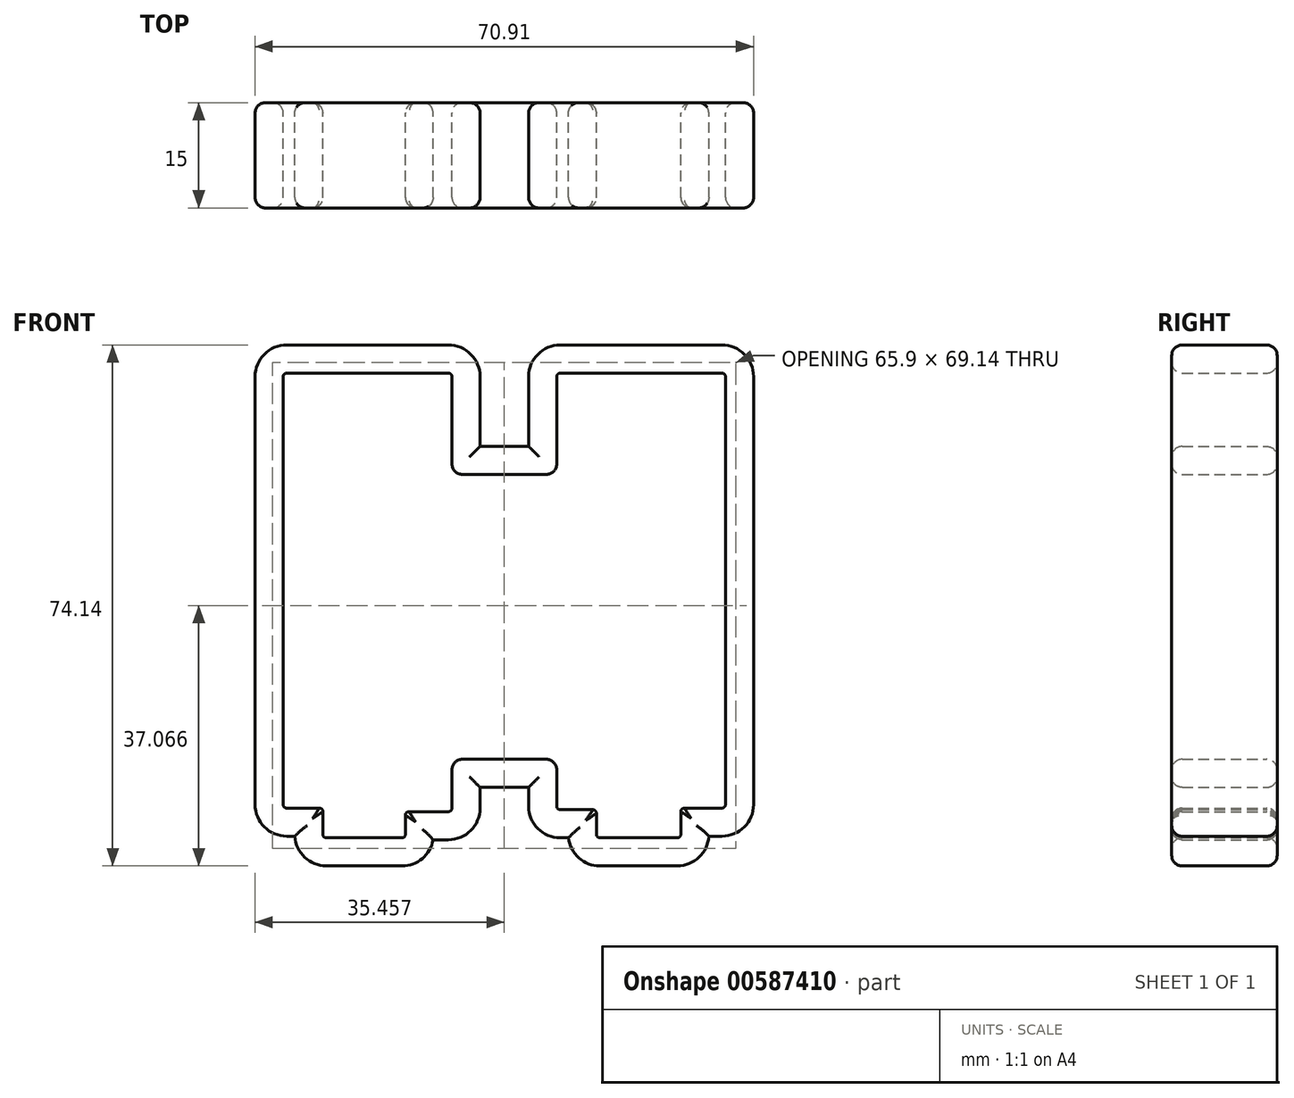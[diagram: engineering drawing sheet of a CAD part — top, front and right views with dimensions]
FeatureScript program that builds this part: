
annotation { "Feature Type Name" : "Feature", "Feature Type Description" : "" }
export const myFeature = defineFeature(function(context is Context, id is Id, definition is map)
    precondition{}
    {
        {
            var Q0;
            Q0=qCreatedBy(makeId("Front.planeOp"),FACE);
            var sketch = newSketch(context, id + "F0", { "sketchPlane" : qUnion([Q0])});
            skLineSegment(sketch, "E0.bottom", {"start": v(-102.27, 13.12) * mm, "end": v(-125.27, 13.12) * mm});
            skLineSegment(sketch, "E0.top", {"start": v(-108.88, -53.02) * mm, "end": v(-119.62, -53.02) * mm});
            skLineSegment(sketch, "E0.left", {"start": v(-101.77, 12.62) * mm, "end": v(-101.77, -48.8) * mm});
            skLineSegment(sketch, "E0.right", {"start": v(-125.77, 12.62) * mm, "end": v(-125.77, -48.28) * mm});
            skLineSegment(sketch, "E1.right", {"start": v(-86.86, -1.3) * mm, "end": v(-86.86, -41.84) * mm});
            skLineSegment(sketch, "E2", {"start": v(-86.86, -1.3) * mm, "end": v(-86.86, 12.62) * mm});
            skLineSegment(sketch, "E3", {"start": v(-86.36, 13.12) * mm, "end": v(-63.36, 13.12) * mm});
            skLineSegment(sketch, "E4", {"start": v(-62.86, 12.62) * mm, "end": v(-62.86, -48.28) * mm});
            skLineSegment(sketch, "E5", {"start": v(-69.71, -53.02) * mm, "end": v(-80.71, -53.02) * mm});
            skLineSegment(sketch, "E6", {"start": v(-86.86, -48.52) * mm, "end": v(-86.86, -41.84) * mm});
            skPoint(sketch, "E7.endSnap0", {"position": v(-113.77, -53.02) * mm});
            skLineSegment(sketch, "E8", {"start": v(-120.12, -49.28) * mm, "end": v(-120.12, -52.52) * mm});
            skLineSegment(sketch, "E9", {"start": v(-108.38, -49.8) * mm, "end": v(-108.38, -52.52) * mm});
            skLineSegment(sketch, "E10", {"start": v(-120.62, -48.78) * mm, "end": v(-125.27, -48.78) * mm});
            skLineSegment(sketch, "E11", {"start": v(-107.88, -49.3) * mm, "end": v(-102.27, -49.3) * mm});
            skPoint(sketch, "E12.orphan", {"position": v(-101.77, -53.02) * mm});
            skPoint(sketch, "E13.orphan", {"position": v(-125.77, -53.02) * mm});
            skPoint(sketch, "E7.end.orphan", {"position": v(-113.77, -49.02) * mm});
            skPoint(sketch, "E7.start.orphan", {"position": v(-113.77, -53.02) * mm});
            skPoint(sketch, "E14.visualSharp", {"position": v(-108.38, -53.02) * mm});
            skArc(sketch, "E14.filletArc", {"start": v(-108.88, -53.02) * mm, "mid": v(-108.53, -52.88) * mm, "end": v(-108.38, -52.52) * mm});
            skPoint(sketch, "E15.visualSharp", {"position": v(-120.12, -53.02) * mm});
            skArc(sketch, "E15.filletArc", {"start": v(-120.12, -52.52) * mm, "mid": v(-119.97, -52.88) * mm, "end": v(-119.62, -53.02) * mm});
            skPoint(sketch, "E16.visualSharp", {"position": v(-120.12, -48.78) * mm});
            skArc(sketch, "E16.filletArc", {"start": v(-120.12, -49.28) * mm, "mid": v(-120.26, -48.93) * mm, "end": v(-120.62, -48.78) * mm});
            skPoint(sketch, "E17.visualSharp", {"position": v(-108.38, -49.3) * mm});
            skArc(sketch, "E17.filletArc", {"start": v(-107.88, -49.3) * mm, "mid": v(-108.24, -49.44) * mm, "end": v(-108.38, -49.8) * mm});
            skPoint(sketch, "E18.visualSharp", {"position": v(-101.77, -49.3) * mm});
            skArc(sketch, "E18.filletArc", {"start": v(-102.27, -49.3) * mm, "mid": v(-101.91, -49.14) * mm, "end": v(-101.77, -48.8) * mm});
            skPoint(sketch, "E19.visualSharp", {"position": v(-125.77, -48.78) * mm});
            skArc(sketch, "E19.filletArc", {"start": v(-125.77, -48.28) * mm, "mid": v(-125.62, -48.64) * mm, "end": v(-125.27, -48.78) * mm});
            skPoint(sketch, "E20.visualSharp", {"position": v(-101.77, 13.12) * mm});
            skArc(sketch, "E20.filletArc", {"start": v(-101.77, 12.62) * mm, "mid": v(-101.91, 12.97) * mm, "end": v(-102.27, 13.12) * mm});
            skPoint(sketch, "E21.visualSharp", {"position": v(-125.77, 13.12) * mm});
            skArc(sketch, "E21.filletArc", {"start": v(-125.27, 13.12) * mm, "mid": v(-125.62, 12.97) * mm, "end": v(-125.77, 12.62) * mm});
            skPoint(sketch, "E22.visualSharp", {"position": v(-86.86, 13.12) * mm});
            skArc(sketch, "E22.filletArc", {"start": v(-86.36, 13.12) * mm, "mid": v(-86.71, 12.97) * mm, "end": v(-86.86, 12.62) * mm});
            skPoint(sketch, "E23.visualSharp", {"position": v(-62.86, 13.12) * mm});
            skArc(sketch, "E23.filletArc", {"start": v(-62.86, 12.62) * mm, "mid": v(-63, 12.97) * mm, "end": v(-63.36, 13.12) * mm});
            skLineSegment(sketch, "E24", {"start": v(-81.21, -49.52) * mm, "end": v(-81.21, -52.52) * mm});
            skLineSegment(sketch, "E25", {"start": v(-69.21, -49.28) * mm, "end": v(-69.21, -52.52) * mm});
            skLineSegment(sketch, "E26", {"start": v(-81.71, -49.02) * mm, "end": v(-86.36, -49.02) * mm});
            skLineSegment(sketch, "E27", {"start": v(-68.71, -48.78) * mm, "end": v(-63.36, -48.78) * mm});
            skPoint(sketch, "E28.start.orphan", {"position": v(-74.86, -53.02) * mm});
            skPoint(sketch, "E29.orphan", {"position": v(-86.86, -53.02) * mm});
            skPoint(sketch, "E30.orphan", {"position": v(-62.86, -53.02) * mm});
            skPoint(sketch, "E31.visualSharp", {"position": v(-81.21, -49.02) * mm});
            skArc(sketch, "E31.filletArc", {"start": v(-81.21, -49.52) * mm, "mid": v(-81.36, -49.17) * mm, "end": v(-81.71, -49.02) * mm});
            skPoint(sketch, "E32.visualSharp", {"position": v(-86.86, -49.02) * mm});
            skArc(sketch, "E32.filletArc", {"start": v(-86.86, -48.52) * mm, "mid": v(-86.71, -48.88) * mm, "end": v(-86.36, -49.02) * mm});
            skPoint(sketch, "E33.visualSharp", {"position": v(-81.21, -53.02) * mm});
            skArc(sketch, "E33.filletArc", {"start": v(-81.21, -52.52) * mm, "mid": v(-81.06, -52.88) * mm, "end": v(-80.71, -53.02) * mm});
            skPoint(sketch, "E34.visualSharp", {"position": v(-69.21, -53.02) * mm});
            skArc(sketch, "E34.filletArc", {"start": v(-69.71, -53.02) * mm, "mid": v(-69.36, -52.88) * mm, "end": v(-69.21, -52.52) * mm});
            skPoint(sketch, "E35.visualSharp", {"position": v(-69.21, -48.78) * mm});
            skArc(sketch, "E35.filletArc", {"start": v(-68.71, -48.78) * mm, "mid": v(-69.06, -48.93) * mm, "end": v(-69.21, -49.28) * mm});
            skPoint(sketch, "E36.visualSharp", {"position": v(-62.86, -48.78) * mm});
            skArc(sketch, "E36.filletArc", {"start": v(-63.36, -48.78) * mm, "mid": v(-63, -48.64) * mm, "end": v(-62.86, -48.28) * mm});
            skLineSegment(sketch, "E37", {"start": v(-101.77, -1.3) * mm, "end": v(-86.86, -1.3) * mm});
            skLineSegment(sketch, "E38", {"start": v(-101.77, -41.84) * mm, "end": v(-86.86, -41.84) * mm});
            skSolve(sketch);
        }
        {
            var Q0;
            Q0 = qSketchRegion(id + "F0", true);
            extrude(context, id + "F1", {"entities" : qUnion([Q0]), "depth" : 15 * mm, "offsetDistance" : 25 * mm});
        }
        {
            var Q0;
            Q0=makeQuery(id+"F1.opExtrude","CAP_FACE",FACE,{"disambiguationData":[OSD([sQuery(id+"F0.wireOp",EDGE,"E0.bottom"),sQuery(id+"F0.wireOp",EDGE,"E0.top"),sQuery(id+"F0.wireOp",EDGE,"E0.left"),sQuery(id+"F0.wireOp",EDGE,"E0.right"),sQuery(id+"F0.wireOp",EDGE,"E2"),sQuery(id+"F0.wireOp",EDGE,"E3"),sQuery(id+"F0.wireOp",EDGE,"E4"),sQuery(id+"F0.wireOp",EDGE,"E5"),sQuery(id+"F0.wireOp",EDGE,"E6"),sQuery(id+"F0.wireOp",EDGE,"E8"),sQuery(id+"F0.wireOp",EDGE,"E9"),sQuery(id+"F0.wireOp",EDGE,"E10"),sQuery(id+"F0.wireOp",EDGE,"E11"),sQuery(id+"F0.wireOp",EDGE,"E14.filletArc"),sQuery(id+"F0.wireOp",EDGE,"E15.filletArc"),sQuery(id+"F0.wireOp",EDGE,"E16.filletArc"),sQuery(id+"F0.wireOp",EDGE,"E17.filletArc"),sQuery(id+"F0.wireOp",EDGE,"E18.filletArc"),sQuery(id+"F0.wireOp",EDGE,"E19.filletArc"),sQuery(id+"F0.wireOp",EDGE,"E20.filletArc"),sQuery(id+"F0.wireOp",EDGE,"E21.filletArc"),sQuery(id+"F0.wireOp",EDGE,"E22.filletArc"),sQuery(id+"F0.wireOp",EDGE,"E23.filletArc"),sQuery(id+"F0.wireOp",EDGE,"E24"),sQuery(id+"F0.wireOp",EDGE,"E25"),sQuery(id+"F0.wireOp",EDGE,"E26"),sQuery(id+"F0.wireOp",EDGE,"E27"),sQuery(id+"F0.wireOp",EDGE,"E31.filletArc"),sQuery(id+"F0.wireOp",EDGE,"E32.filletArc"),sQuery(id+"F0.wireOp",EDGE,"E33.filletArc"),sQuery(id+"F0.wireOp",EDGE,"E34.filletArc"),sQuery(id+"F0.wireOp",EDGE,"E35.filletArc"),sQuery(id+"F0.wireOp",EDGE,"E36.filletArc"),sQuery(id+"F0.wireOp",EDGE,"E37"),sQuery(id+"F0.wireOp",EDGE,"E38")])],"isStart":true});
            var Q1;
            Q1=makeQuery(id+"F1.opExtrude","CAP_FACE",FACE,{"disambiguationData":[OSD([sQuery(id+"F0.wireOp",EDGE,"E0.bottom"),sQuery(id+"F0.wireOp",EDGE,"E0.top"),sQuery(id+"F0.wireOp",EDGE,"E0.left"),sQuery(id+"F0.wireOp",EDGE,"E0.right"),sQuery(id+"F0.wireOp",EDGE,"E2"),sQuery(id+"F0.wireOp",EDGE,"E3"),sQuery(id+"F0.wireOp",EDGE,"E4"),sQuery(id+"F0.wireOp",EDGE,"E5"),sQuery(id+"F0.wireOp",EDGE,"E6"),sQuery(id+"F0.wireOp",EDGE,"E8"),sQuery(id+"F0.wireOp",EDGE,"E9"),sQuery(id+"F0.wireOp",EDGE,"E10"),sQuery(id+"F0.wireOp",EDGE,"E11"),sQuery(id+"F0.wireOp",EDGE,"E14.filletArc"),sQuery(id+"F0.wireOp",EDGE,"E15.filletArc"),sQuery(id+"F0.wireOp",EDGE,"E16.filletArc"),sQuery(id+"F0.wireOp",EDGE,"E17.filletArc"),sQuery(id+"F0.wireOp",EDGE,"E18.filletArc"),sQuery(id+"F0.wireOp",EDGE,"E19.filletArc"),sQuery(id+"F0.wireOp",EDGE,"E20.filletArc"),sQuery(id+"F0.wireOp",EDGE,"E21.filletArc"),sQuery(id+"F0.wireOp",EDGE,"E22.filletArc"),sQuery(id+"F0.wireOp",EDGE,"E23.filletArc"),sQuery(id+"F0.wireOp",EDGE,"E24"),sQuery(id+"F0.wireOp",EDGE,"E25"),sQuery(id+"F0.wireOp",EDGE,"E26"),sQuery(id+"F0.wireOp",EDGE,"E27"),sQuery(id+"F0.wireOp",EDGE,"E31.filletArc"),sQuery(id+"F0.wireOp",EDGE,"E32.filletArc"),sQuery(id+"F0.wireOp",EDGE,"E33.filletArc"),sQuery(id+"F0.wireOp",EDGE,"E34.filletArc"),sQuery(id+"F0.wireOp",EDGE,"E35.filletArc"),sQuery(id+"F0.wireOp",EDGE,"E36.filletArc"),sQuery(id+"F0.wireOp",EDGE,"E37"),sQuery(id+"F0.wireOp",EDGE,"E38")])],"isStart":false});
            shell(context, id + "F2", {"entities" : qUnion([Q0, Q1]), "thickness" : 4 * mm, "oppositeDirection" : true});
        }
        {
            var Q0;
            Q0=makeQuery(id+"F1.opExtrude","SWEPT_FACE",FACE,{"disambiguationData":[OSD([sQuery(id+"F0.wireOp",EDGE,"E0.top")])]});
            var Q1;
            Q1=makeQuery(id+"F1.opExtrude","SWEPT_FACE",FACE,{"disambiguationData":[OSD([sQuery(id+"F0.wireOp",EDGE,"E5")])]});
            var Q2;
            Q2=makeQuery(id+"F1.opExtrude","SWEPT_FACE",FACE,{"disambiguationData":[OSD([sQuery(id+"F0.wireOp",EDGE,"E36.filletArc")])]});
            var Q3;
            Q3=makeQuery(id+"F1.opExtrude","SWEPT_FACE",FACE,{"disambiguationData":[OSD([sQuery(id+"F0.wireOp",EDGE,"E32.filletArc")])]});
            var Q4;
            Q4=makeQuery(id+"F1.opExtrude","SWEPT_FACE",FACE,{"disambiguationData":[OSD([sQuery(id+"F0.wireOp",EDGE,"E18.filletArc")])]});
            var Q5;
            Q5=makeQuery(id+"F1.opExtrude","SWEPT_FACE",FACE,{"disambiguationData":[OSD([sQuery(id+"F0.wireOp",EDGE,"E19.filletArc")])]});
            var Q6;
            Q6=makeQuery(id+"F1.opExtrude","CAP_FACE",FACE,{"disambiguationData":[OSD([sQuery(id+"F0.wireOp",EDGE,"E0.bottom"),sQuery(id+"F0.wireOp",EDGE,"E0.top"),sQuery(id+"F0.wireOp",EDGE,"E0.left"),sQuery(id+"F0.wireOp",EDGE,"E0.right"),sQuery(id+"F0.wireOp",EDGE,"E2"),sQuery(id+"F0.wireOp",EDGE,"E3"),sQuery(id+"F0.wireOp",EDGE,"E4"),sQuery(id+"F0.wireOp",EDGE,"E5"),sQuery(id+"F0.wireOp",EDGE,"E6"),sQuery(id+"F0.wireOp",EDGE,"E8"),sQuery(id+"F0.wireOp",EDGE,"E9"),sQuery(id+"F0.wireOp",EDGE,"E10"),sQuery(id+"F0.wireOp",EDGE,"E11"),sQuery(id+"F0.wireOp",EDGE,"E14.filletArc"),sQuery(id+"F0.wireOp",EDGE,"E15.filletArc"),sQuery(id+"F0.wireOp",EDGE,"E16.filletArc"),sQuery(id+"F0.wireOp",EDGE,"E17.filletArc"),sQuery(id+"F0.wireOp",EDGE,"E18.filletArc"),sQuery(id+"F0.wireOp",EDGE,"E19.filletArc"),sQuery(id+"F0.wireOp",EDGE,"E20.filletArc"),sQuery(id+"F0.wireOp",EDGE,"E21.filletArc"),sQuery(id+"F0.wireOp",EDGE,"E22.filletArc"),sQuery(id+"F0.wireOp",EDGE,"E23.filletArc"),sQuery(id+"F0.wireOp",EDGE,"E24"),sQuery(id+"F0.wireOp",EDGE,"E25"),sQuery(id+"F0.wireOp",EDGE,"E26"),sQuery(id+"F0.wireOp",EDGE,"E27"),sQuery(id+"F0.wireOp",EDGE,"E31.filletArc"),sQuery(id+"F0.wireOp",EDGE,"E32.filletArc"),sQuery(id+"F0.wireOp",EDGE,"E33.filletArc"),sQuery(id+"F0.wireOp",EDGE,"E34.filletArc"),sQuery(id+"F0.wireOp",EDGE,"E35.filletArc"),sQuery(id+"F0.wireOp",EDGE,"E36.filletArc"),sQuery(id+"F0.wireOp",EDGE,"E37"),sQuery(id+"F0.wireOp",EDGE,"E38")])],"isStart":true});
            var Q7;
            Q7=makeQuery(id+"F1.opExtrude","CAP_FACE",FACE,{"disambiguationData":[OSD([sQuery(id+"F0.wireOp",EDGE,"E0.bottom"),sQuery(id+"F0.wireOp",EDGE,"E0.top"),sQuery(id+"F0.wireOp",EDGE,"E0.left"),sQuery(id+"F0.wireOp",EDGE,"E0.right"),sQuery(id+"F0.wireOp",EDGE,"E2"),sQuery(id+"F0.wireOp",EDGE,"E3"),sQuery(id+"F0.wireOp",EDGE,"E4"),sQuery(id+"F0.wireOp",EDGE,"E5"),sQuery(id+"F0.wireOp",EDGE,"E6"),sQuery(id+"F0.wireOp",EDGE,"E8"),sQuery(id+"F0.wireOp",EDGE,"E9"),sQuery(id+"F0.wireOp",EDGE,"E10"),sQuery(id+"F0.wireOp",EDGE,"E11"),sQuery(id+"F0.wireOp",EDGE,"E14.filletArc"),sQuery(id+"F0.wireOp",EDGE,"E15.filletArc"),sQuery(id+"F0.wireOp",EDGE,"E16.filletArc"),sQuery(id+"F0.wireOp",EDGE,"E17.filletArc"),sQuery(id+"F0.wireOp",EDGE,"E18.filletArc"),sQuery(id+"F0.wireOp",EDGE,"E19.filletArc"),sQuery(id+"F0.wireOp",EDGE,"E20.filletArc"),sQuery(id+"F0.wireOp",EDGE,"E21.filletArc"),sQuery(id+"F0.wireOp",EDGE,"E22.filletArc"),sQuery(id+"F0.wireOp",EDGE,"E23.filletArc"),sQuery(id+"F0.wireOp",EDGE,"E24"),sQuery(id+"F0.wireOp",EDGE,"E25"),sQuery(id+"F0.wireOp",EDGE,"E26"),sQuery(id+"F0.wireOp",EDGE,"E27"),sQuery(id+"F0.wireOp",EDGE,"E31.filletArc"),sQuery(id+"F0.wireOp",EDGE,"E32.filletArc"),sQuery(id+"F0.wireOp",EDGE,"E33.filletArc"),sQuery(id+"F0.wireOp",EDGE,"E34.filletArc"),sQuery(id+"F0.wireOp",EDGE,"E35.filletArc"),sQuery(id+"F0.wireOp",EDGE,"E36.filletArc"),sQuery(id+"F0.wireOp",EDGE,"E37"),sQuery(id+"F0.wireOp",EDGE,"E38")])],"isStart":false});
            var Q8;
            Q8=makeQuery(id+"F2.opShell","OFFSET_FACE",FACE,{"disambiguationData":[OSD([sQuery(id+"F0.wireOp",EDGE,"E37")])]});
            var Q9;
            Q9=makeQuery(id+"F2.opShell","OFFSET_FACE",FACE,{"disambiguationData":[OSD([sQuery(id+"F0.wireOp",EDGE,"E38")])]});
            fillet(context, id + "F3", {"entities" : qUnion([Q0, Q1, Q2, Q3, Q4, Q5, Q6, Q7, Q8, Q9]), "radius" : 1.5 * mm, "tangentPropagation" : true, "allowEdgeOverflow" : false});
        }
    });
